# Revit family: Toilet_Seat-Elongated_Closed_Front-Cleansing-KOHLER-Purewash-K-28820K
name_source: partatom
category: Plumbing Fixtures
units: mm (PartAtom-declared; Revit-internal decimal feet)

## family parameters
Cut with Voids When Loaded = No
Host = Face
OmniClass Number = 23.31.19.19.17
OmniClass Title = Water Closet Seats
Part Type = Normal
Room Calculation Point = No
Round Connector Dimension = Use Diameter
Shared = No

## types (1)
- 0-White
    ADA Compliant = No
    Apparent Load = 1200 VA
    Assembly Code = D2010100
    CW Connection = Yes
    Cold Water Inlet = Cold Water Inlet
    Date Modified = 11/18/2023
    Default Elevation = 15"
    Description = E900 Round Bidet Seat
    Electrical Connector = Yes
    Electrical Note = One Dedicated Circuit Required
    Finish = Kohler-Plastic-0-White
    Flow Rate = 0 GPM
    Flush Rate- GPF = 0 GPF
    Flush Rate- LPF = 0 LPF
    HW Connection = No
    Height = 3 9/16"
    Hot Water Inlet = Hot Water Inlet
    Length = 20 1/4"
    Manufacturer = Kohler Co.
    Master Format 2014 = 22 41 13.13
    Master Format 2014 Name = Residential Water Closets
    Material = Plastic Construction
    Model = K-28820K-0
    Pressure = 0.00 psi
    Product Name = Purewash
    Seat Included = Yes
    Type = 1
    URL = https://www.kohlerasiapacific.com
    Vent Connection = No
    Voltage = 120 V
    Waste Connection = No
    Waste Water Outlet = Waste Water Outlet
    WaterSense Certified = No
    Width = 15 1/16"

## geometry (parser evidence)
native form markers: Sweep x4
no freeform markers — native parametric forms only
